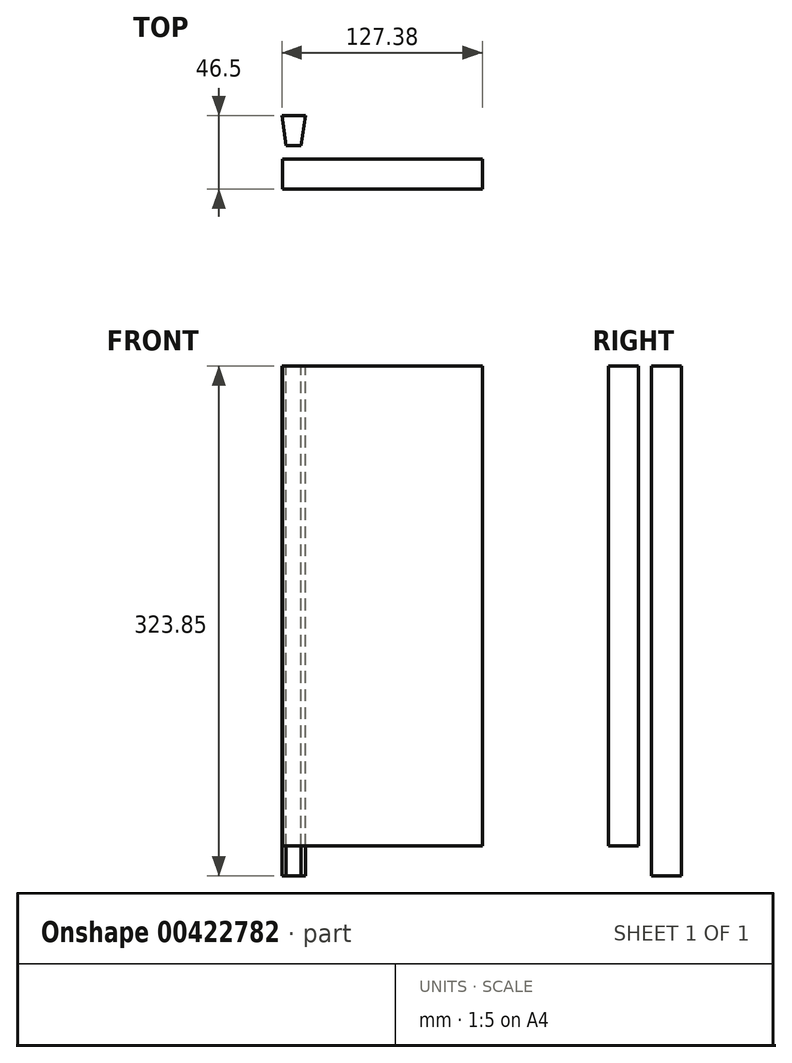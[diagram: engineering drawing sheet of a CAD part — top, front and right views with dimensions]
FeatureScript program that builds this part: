
annotation { "Feature Type Name" : "Feature", "Feature Type Description" : "" }
export const myFeature = defineFeature(function(context is Context, id is Id, definition is map)
    precondition{}
    {
        {
            var Q0;
            Q0=qCreatedBy(makeId("Top.planeOp"),FACE);
            var sketch = newSketch(context, id + "F0", { "sketchPlane" : qUnion([Q0])});
            skLineSegment(sketch, "E0", {"start": v(-57.52, 36.87) * mm, "end": v(-42.57, 36.87) * mm});
            skLineSegment(sketch, "E1", {"start": v(-42.57, 36.87) * mm, "end": v(-45.25, 17.82) * mm});
            skLineSegment(sketch, "E2", {"start": v(-45.25, 17.82) * mm, "end": v(-54.85, 17.82) * mm});
            skLineSegment(sketch, "E3", {"start": v(-54.85, 17.82) * mm, "end": v(-57.52, 36.87) * mm});
            skLineSegment(sketch, "E4", {"start": v(-42.57, 36.87) * mm, "end": v(-42.57, -8.07) * mm, "construction": true});
            skLineSegment(sketch, "E5", {"start": v(-57.52, 36.87) * mm, "end": v(-57.52, -7) * mm, "construction": true});
            skLineSegment(sketch, "E6", {"start": v(-45.25, 17.82) * mm, "end": v(-29.84, 17.82) * mm, "construction": true});
            skLineSegment(sketch, "E7", {"start": v(-42.57, 36.87) * mm, "end": v(4.78, 36.87) * mm, "construction": true});
            skSolve(sketch);
        }
        {
            var Q0;
            Q0=makeQuery(id+"F0.imprint","IMPRINT",FACE,{"disambiguationData":[TD([[makeQuery(id+"F0.imprint","IMPRINT",EDGE,{"derivedFrom":sQuery(id+"F0.wireOp",EDGE,"E0")}),-1.0]])]});
            extrude(context, id + "F1", {"entities" : qUnion([Q0]), "oppositeDirection" : true, "depth" : 19.05 * mm});
        }
        {
            var Q0;
            Q0=qCreatedBy(makeId("Top.planeOp"),FACE);
            var sketch = newSketch(context, id + "F2", { "sketchPlane" : qUnion([Q0])});
            skLineSegment(sketch, "E8", {"start": v(-57.14, 9.42) * mm, "end": v(69.86, 9.42) * mm});
            skLineSegment(sketch, "E9", {"start": v(69.86, 9.42) * mm, "end": v(69.86, -9.63) * mm});
            skLineSegment(sketch, "E10", {"start": v(69.86, -9.63) * mm, "end": v(-57.14, -9.63) * mm});
            skLineSegment(sketch, "E11", {"start": v(-57.14, -9.63) * mm, "end": v(-57.14, 9.42) * mm});
            skSolve(sketch);
        }
        {
            var Q0;
            Q0=makeQuery(id+"F1.opExtrude","CAP_FACE",FACE,{"disambiguationData":[OSD([sQuery(id+"F0.wireOp",EDGE,"E0"),sQuery(id+"F0.wireOp",EDGE,"E1"),sQuery(id+"F0.wireOp",EDGE,"E2"),sQuery(id+"F0.wireOp",EDGE,"E3")])],"isStart":false});
            var Q1;
            Q1=makeQuery(id+"F2.imprint","IMPRINT",FACE,{"disambiguationData":[TD([[makeQuery(id+"F2.imprint","IMPRINT",EDGE,{"derivedFrom":sQuery(id+"F2.wireOp",EDGE,"E8")}),-1.0]])]});
            extrude(context, id + "F3", {"entities" : qUnion([Q0, Q1]), "operationType" : NewBodyOperationType.ADD, "depth" : 304.8 * mm});
        }
    });
